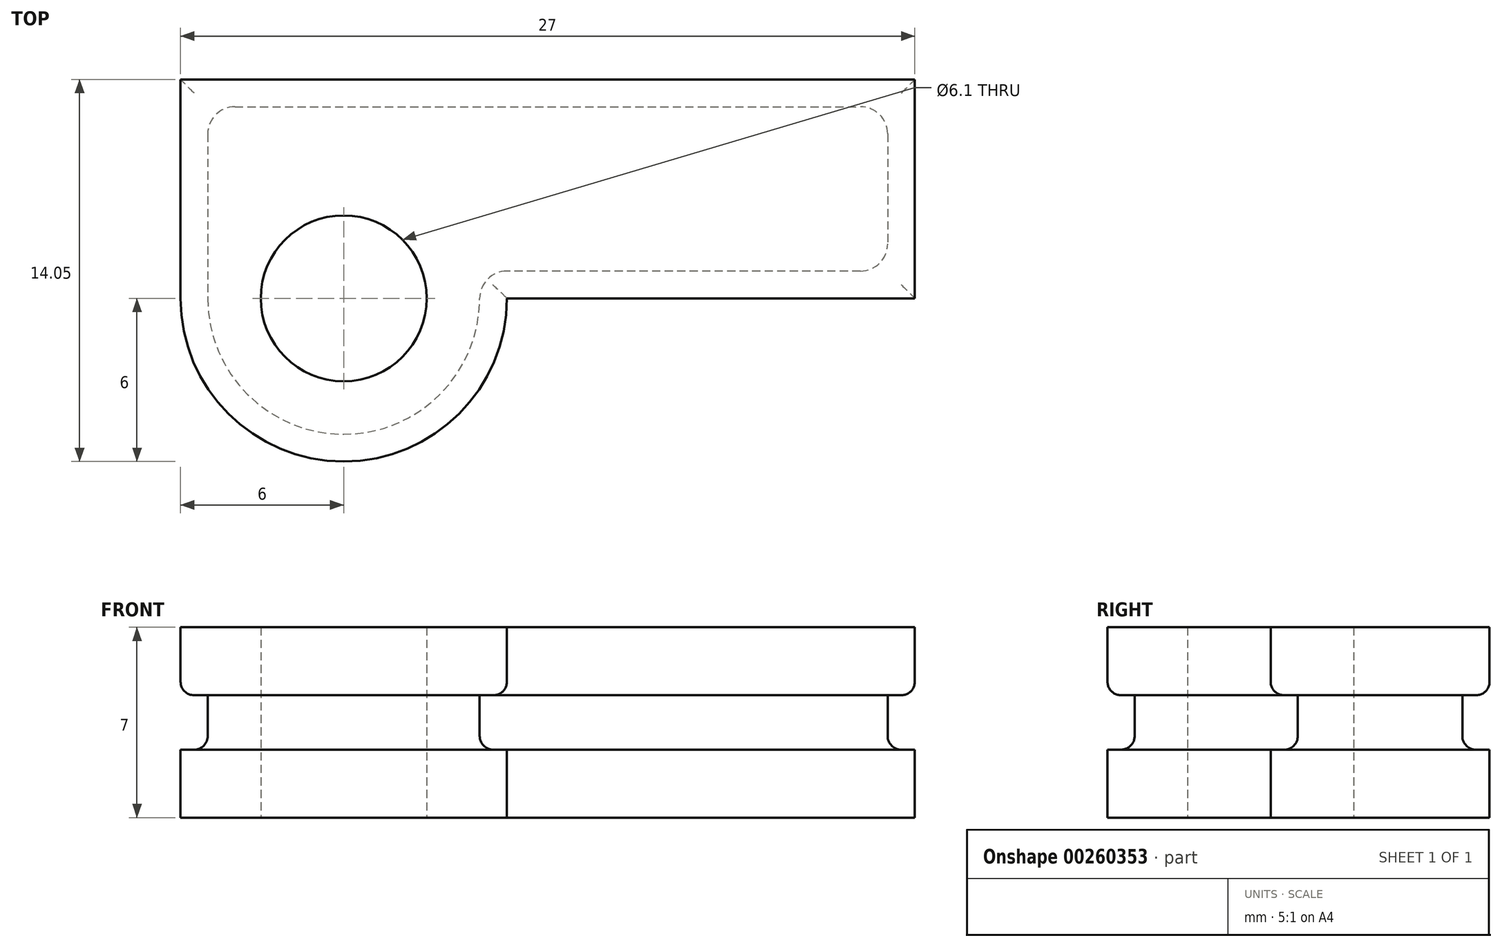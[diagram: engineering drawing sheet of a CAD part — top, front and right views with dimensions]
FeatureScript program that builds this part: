
annotation { "Feature Type Name" : "Feature", "Feature Type Description" : "" }
export const myFeature = defineFeature(function(context is Context, id is Id, definition is map)
    precondition{}
    {
        {
            var Q0;
            Q0=qCreatedBy(makeId("Top.planeOp"),FACE);
            var sketch = newSketch(context, id + "F0", { "sketchPlane" : qUnion([Q0])});
            skCircle(sketch, "E0", {"center": v(0, 0) * mm, "radius": 3.05 * mm});
            skLineSegment(sketch, "E1.bottom", {"start": v(6, 8.05) * mm, "end": v(-6, 8.05) * mm});
            skLineSegment(sketch, "E2", {"start": v(0, 3.05) * mm, "end": v(6, 3.05) * mm, "construction": true});
            skLineSegment(sketch, "E3", {"start": v(-6, 8.05) * mm, "end": v(-6, 0) * mm});
            skArc(sketch, "E4", {"start": v(-6, 0) * mm, "mid": v(0, -6) * mm, "end": v(6, 0) * mm});
            skLineSegment(sketch, "E5", {"start": v(6, 8.05) * mm, "end": v(6, 0) * mm, "construction": true});
            skLineSegment(sketch, "E6", {"start": v(6, 8.05) * mm, "end": v(21, 8.05) * mm});
            skLineSegment(sketch, "E7", {"start": v(21, 8.05) * mm, "end": v(21, 0) * mm});
            skLineSegment(sketch, "E8", {"start": v(21, 0) * mm, "end": v(6, 0) * mm});
            skSolve(sketch);
        }
        {
            var Q0;
            Q0 = qSketchRegion(id + "F0", true);
            extrude(context, id + "F1", {"entities" : qUnion([Q0]), "depth" : 7 * mm});
        }
        {
            var Q0;
            Q0=makeQuery(id+"F1.opExtrude","CAP_FACE",FACE,{"disambiguationData":[OSD([sQuery(id+"F0.wireOp",EDGE,"E0"),sQuery(id+"F0.wireOp",EDGE,"E1.bottom"),sQuery(id+"F0.wireOp",EDGE,"E3"),sQuery(id+"F0.wireOp",EDGE,"E4"),sQuery(id+"F0.wireOp",EDGE,"E5")])],"isStart":false});
            var sketch = newSketch(context, id + "F2", { "sketchPlane" : qUnion([Q0])});
            skLineSegment(sketch, "E9", {"start": v(-6, 0) * mm, "end": v(-6, 0) * mm});
            skLineSegment(sketch, "E10", {"start": v(-4, 7.05) * mm, "end": v(19, 7.05) * mm});
            skLineSegment(sketch, "E11", {"start": v(20, 6.05) * mm, "end": v(20, 2) * mm});
            skLineSegment(sketch, "E12", {"start": v(19, 1) * mm, "end": v(6, 1) * mm});
            skLineSegment(sketch, "E13", {"start": v(-5, 6.05) * mm, "end": v(-5, 0) * mm});
            skArc(sketch, "E14", {"start": v(-5, 0) * mm, "mid": v(0, -5) * mm, "end": v(5, 0) * mm});
            skLineSegment(sketch, "E15", {"start": v(5, 0) * mm, "end": v(5, 0) * mm});
            skPoint(sketch, "E16.visualSharp", {"position": v(-5, 7.05) * mm});
            skArc(sketch, "E16.filletArc", {"start": v(-4, 7.05) * mm, "mid": v(-4.7, 6.76) * mm, "end": v(-5, 6.05) * mm});
            skPoint(sketch, "E17.visualSharp", {"position": v(20, 7.05) * mm});
            skArc(sketch, "E17.filletArc", {"start": v(20, 6.05) * mm, "mid": v(19.7, 6.76) * mm, "end": v(19, 7.05) * mm});
            skPoint(sketch, "E18.visualSharp", {"position": v(20, 1) * mm});
            skArc(sketch, "E18.filletArc", {"start": v(19, 1) * mm, "mid": v(19.7, 1.3) * mm, "end": v(20, 2) * mm});
            skPoint(sketch, "E19.visualSharp", {"position": v(5, 1) * mm});
            skArc(sketch, "E19.filletArc", {"start": v(6, 1) * mm, "mid": v(5.3, 0.7) * mm, "end": v(5, 0) * mm});
            skLineSegment(sketch, "E20", {"start": v(-6, 8.05) * mm, "end": v(21, 8.05) * mm});
            skLineSegment(sketch, "E21", {"start": v(21, 8.05) * mm, "end": v(21, 0) * mm});
            skLineSegment(sketch, "E22", {"start": v(21, 0) * mm, "end": v(6, 0) * mm});
            skLineSegment(sketch, "E23", {"start": v(-6, 8.05) * mm, "end": v(-6, 0) * mm});
            skArc(sketch, "E24", {"start": v(-6, 0) * mm, "mid": v(0, -6) * mm, "end": v(6, 0) * mm});
            skSolve(sketch);
        }
        {
            var Q0;
            Q0=makeQuery(id+"F2.imprint","IMPRINT",FACE,{"disambiguationData":[TD([[makeQuery(id+"F2.imprint","IMPRINT",EDGE,{"derivedFrom":sQuery(id+"F2.wireOp",EDGE,"E10")}),1.0]])]});
            extrude(context, id + "F3", {"entities" : qUnion([Q0]), "operationType" : NewBodyOperationType.REMOVE, "oppositeDirection" : true, "depth" : 4.5 * mm});
        }
        {
            var Q0;
            Q0=makeQuery(id+"F2.imprint","IMPRINT",FACE,{"disambiguationData":[TD([[makeQuery(id+"F2.imprint","IMPRINT",EDGE,{"derivedFrom":sQuery(id+"F2.wireOp",EDGE,"l8Qsqhbn-USzY-feL4-Y05h-HQRm95NpL2UF")}),-1.0]])]});
            var Q1;
            Q1=makeQuery(id+"F2.imprint","IMPRINT",FACE,{"disambiguationData":[TD([[makeQuery(id+"F2.imprint","IMPRINT",EDGE,{"derivedFrom":sQuery(id+"F2.wireOp",EDGE,"E10")}),1.0]])]});
            extrude(context, id + "F4", {"entities" : qUnion([Q0, Q1]), "operationType" : NewBodyOperationType.ADD, "oppositeDirection" : true, "depth" : 2.5 * mm});
        }
        {
            var Q0;
            Q0=makeQuery(id+"F4.opExtrude","CAP_EDGE",EDGE,{"disambiguationData":[OSD([sQuery(id+"F2.wireOp",EDGE,"E14")])],"isStart":false});
            var Q1;
            Q1=makeQuery(id+"F3.boolean.opBoolean","COPY",EDGE,{"derivedFrom":makeQuery(id+"F3.opExtrude","CAP_EDGE",EDGE,{"disambiguationData":[OSD([sQuery(id+"F2.wireOp",EDGE,"E14")])],"isStart":false})});
            fillet(context, id + "F5", {"entities" : qUnion([Q0, Q1]), "radius" : 0.5 * mm, "tangentPropagation" : true, "allowEdgeOverflow" : false});
        }
        {
            var Q0;
            Q0=makeQuery(id+"F4.opExtrude","CAP_EDGE",EDGE,{"disambiguationData":[OSD([sQuery(id+"F2.wireOp",EDGE,"E23")])],"isStart":false});
            var Q1;
            Q1=makeQuery(id+"F3.boolean.opBoolean","COPY",EDGE,{"derivedFrom":makeQuery(id+"F3.opExtrude","CAP_EDGE",EDGE,{"disambiguationData":[OSD([sQuery(id+"F2.wireOp",EDGE,"E23")])],"isStart":false})});
            var Q2;
            Q2=makeQuery(id+"F3.boolean.opBoolean","COPY",EDGE,{"derivedFrom":makeQuery(id+"F3.opExtrude","CAP_EDGE",EDGE,{"disambiguationData":[OSD([sQuery(id+"F2.wireOp",EDGE,"E22")])],"isStart":false})});
            var Q3;
            Q3=makeQuery(id+"F3.boolean.opBoolean","COPY",EDGE,{"derivedFrom":makeQuery(id+"F3.opExtrude","CAP_EDGE",EDGE,{"disambiguationData":[OSD([sQuery(id+"F2.wireOp",EDGE,"E21")])],"isStart":false})});
            var Q4;
            Q4=makeQuery(id+"F4.opExtrude","CAP_EDGE",EDGE,{"disambiguationData":[OSD([sQuery(id+"F2.wireOp",EDGE,"E22")])],"isStart":false});
            var Q5;
            Q5=makeQuery(id+"F4.opExtrude","CAP_EDGE",EDGE,{"disambiguationData":[OSD([sQuery(id+"F2.wireOp",EDGE,"E20")])],"isStart":false});
            var Q6;
            Q6=makeQuery(id+"F3.boolean.opBoolean","COPY",EDGE,{"derivedFrom":makeQuery(id+"F3.opExtrude","CAP_EDGE",EDGE,{"disambiguationData":[OSD([sQuery(id+"F2.wireOp",EDGE,"E20")])],"isStart":false})});
            var Q7;
            Q7=makeQuery(id+"F4.opExtrude","CAP_EDGE",EDGE,{"disambiguationData":[OSD([sQuery(id+"F2.wireOp",EDGE,"E21")])],"isStart":false});
            fillet(context, id + "F6", {"entities" : qUnion([Q0, Q1, Q2, Q3, Q4, Q5, Q6, Q7]), "radius" : 0.5 * mm, "tangentPropagation" : true, "allowEdgeOverflow" : false});
        }
    });
